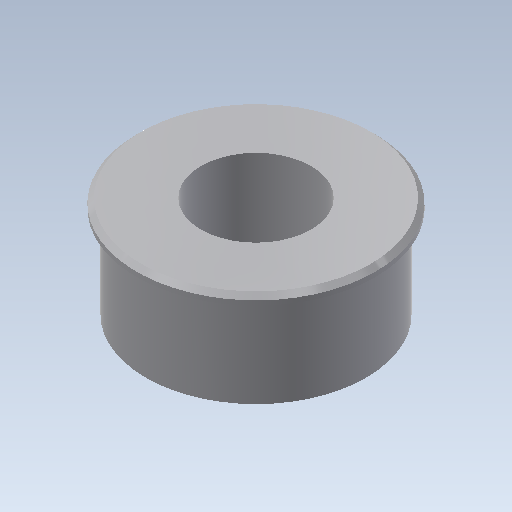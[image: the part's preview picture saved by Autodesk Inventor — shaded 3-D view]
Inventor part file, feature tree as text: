
AUTODESK INVENTOR PART (.ipt)
format: ipt  version: 2020 (Build 240168000, 168)  size: 107,008 bytes
history: native  units: mm
features: extrude x3, sketch x3, chamfer x1
ambient origin geometry x8: Origin, YZ Plane, XZ Plane, XY Plane, X Axis, Y Axis, Z Axis, Center Point
bodies: Solid1 (feature_tree)
feature tree (7):
  extrude  "Extrusion1"  Depth=5.0mm TaperAngle=0.0deg
  extrude  "Extrusion2"  Depth=0.5mm TaperAngle=0.0deg
  chamfer  "Chamfer1"  Distance=0.25mm Angle=45.0deg
  extrude  "Extrusion3"  Depth=0.5mm TaperAngle=0.0deg
  sketch  "Sketch1"  dims[d0=12.0mm d1=5.0mm d2=0.0mm]
  sketch  "Sketch2"  dims[d3=13.0mm d4=0.5mm d5=0.0mm d6=0.25mm d7=2.0mm d8=45.0deg]
  sketch  "Sketch3"  dims[d9=6.0mm d10=0.5mm d11=0.0mm]
